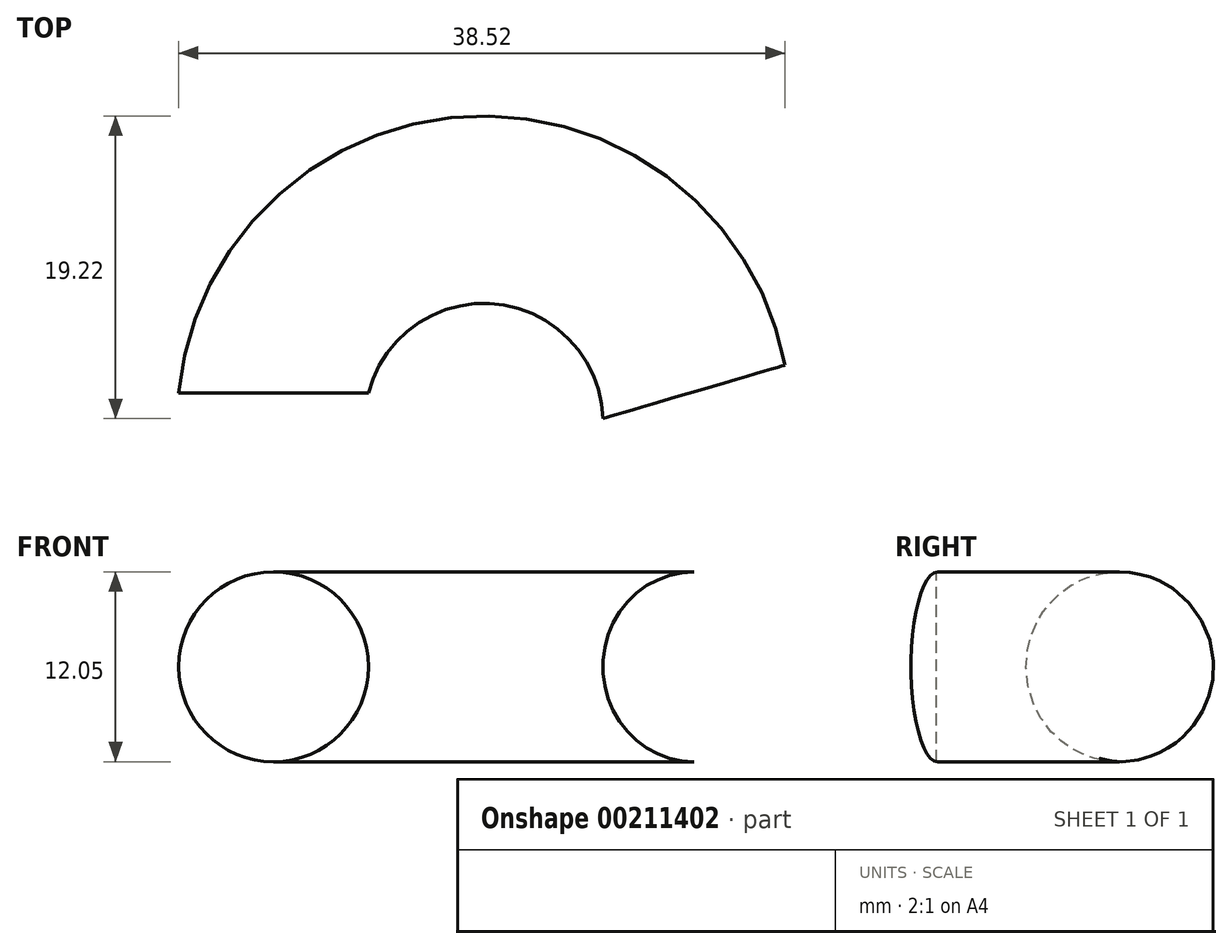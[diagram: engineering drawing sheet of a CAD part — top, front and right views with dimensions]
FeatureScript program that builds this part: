
annotation { "Feature Type Name" : "Feature", "Feature Type Description" : "" }
export const myFeature = defineFeature(function(context is Context, id is Id, definition is map)
    precondition{}
    {
        {
            var Q0;
            Q0=qCreatedBy(makeId("Front.planeOp"),FACE);
            var sketch = newSketch(context, id + "F0", { "sketchPlane" : qUnion([Q0])});
            skCircle(sketch, "E0", {"center": v(-3.96, 4.55) * mm, "radius": 6.03 * mm});
            skSolve(sketch);
        }
        {
            var Q0;
            Q0=qCreatedBy(makeId("Top.planeOp"),FACE);
            var sketch = newSketch(context, id + "F1", { "sketchPlane" : qUnion([Q0])});
            skArc(sketch, "E1", {"start": v(22.49, 0) * mm, "mid": v(9.4, 11.34) * mm, "end": v(-3.69, 0) * mm});
            skSolve(sketch);
        }
        {
            var Q0;
            Q0=makeQuery(id+"F0.imprint","IMPRINT",FACE,{"disambiguationData":[TD([[makeQuery(id+"F0.imprint","IMPRINT",EDGE,{"derivedFrom":sQuery(id+"F0.wireOp",EDGE,"E0")}),1.0]])]});
            var Q1;
            Q1=sQuery(id+"F1.wireOp",EDGE,"E1");
            sweep(context, id + "F2", {"profiles" : qUnion([Q0]), "path" : qUnion([Q1])});
        }
    });
